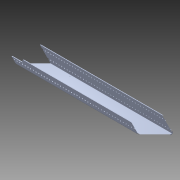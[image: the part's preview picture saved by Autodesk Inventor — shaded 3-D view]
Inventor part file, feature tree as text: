
AUTODESK INVENTOR PART (.ipt)
format: ipt  version: 2015 SP1 (Build 190203100, 203)  size: 520,192 bytes
history: native  units: in
note: dims shown in document units (in); Inventor stores cm internally (conversion verified against a paired STEP export)
features: projected_geometry x8, extrude x3, sketch x3, other x2, chamfer x2, imported_body x1
ambient origin geometry x8: Origin, YZ Plane, XZ Plane, XY Plane, X Axis, Y Axis, Z Axis, Center Point
bodies: Body1 (feature_tree)
feature tree (19):
  other  "LPattern4"
  other  "AM14U2 End Sheet1"
  extrude  "Extrusion1"  Depth=0.125in TaperAngle=45.0deg
  chamfer  "Chamfer1"  Distance=0.75in
  extrude  "Extrusion2"  Depth=2.25in
  chamfer  "Chamfer2"  Distance=0.75in
  extrude  "Extrusion3"  Depth=0.5in
  imported_body  "Base1"
  sketch  "Sketch1"  dims[d0=4.0in d1=0.0in d2=0.125in d3=0.125in d4=45.0deg]
  projected_geometry  "Projected Loop1"
  projected_geometry  "Projected Loop2"
  projected_geometry  "Projected Loop3"
  projected_geometry  "Projected Loop4"
  projected_geometry  "Projected Loop5"
  projected_geometry  "Projected Loop6"
  projected_geometry  "Projected Loop7"
  sketch  "Sketch2"  dims[d5=2.25in]
  projected_geometry  "Projected Loop8"
  sketch  "Sketch3"  dims[d6=0.5in d7=0.75in d8=2.25in d9=0.75in d10=0.5in d11=1.0in d12=0.0in d13=0.125in d14=0.125in d15=45.0deg d16=1.0in d17=0.0in]
